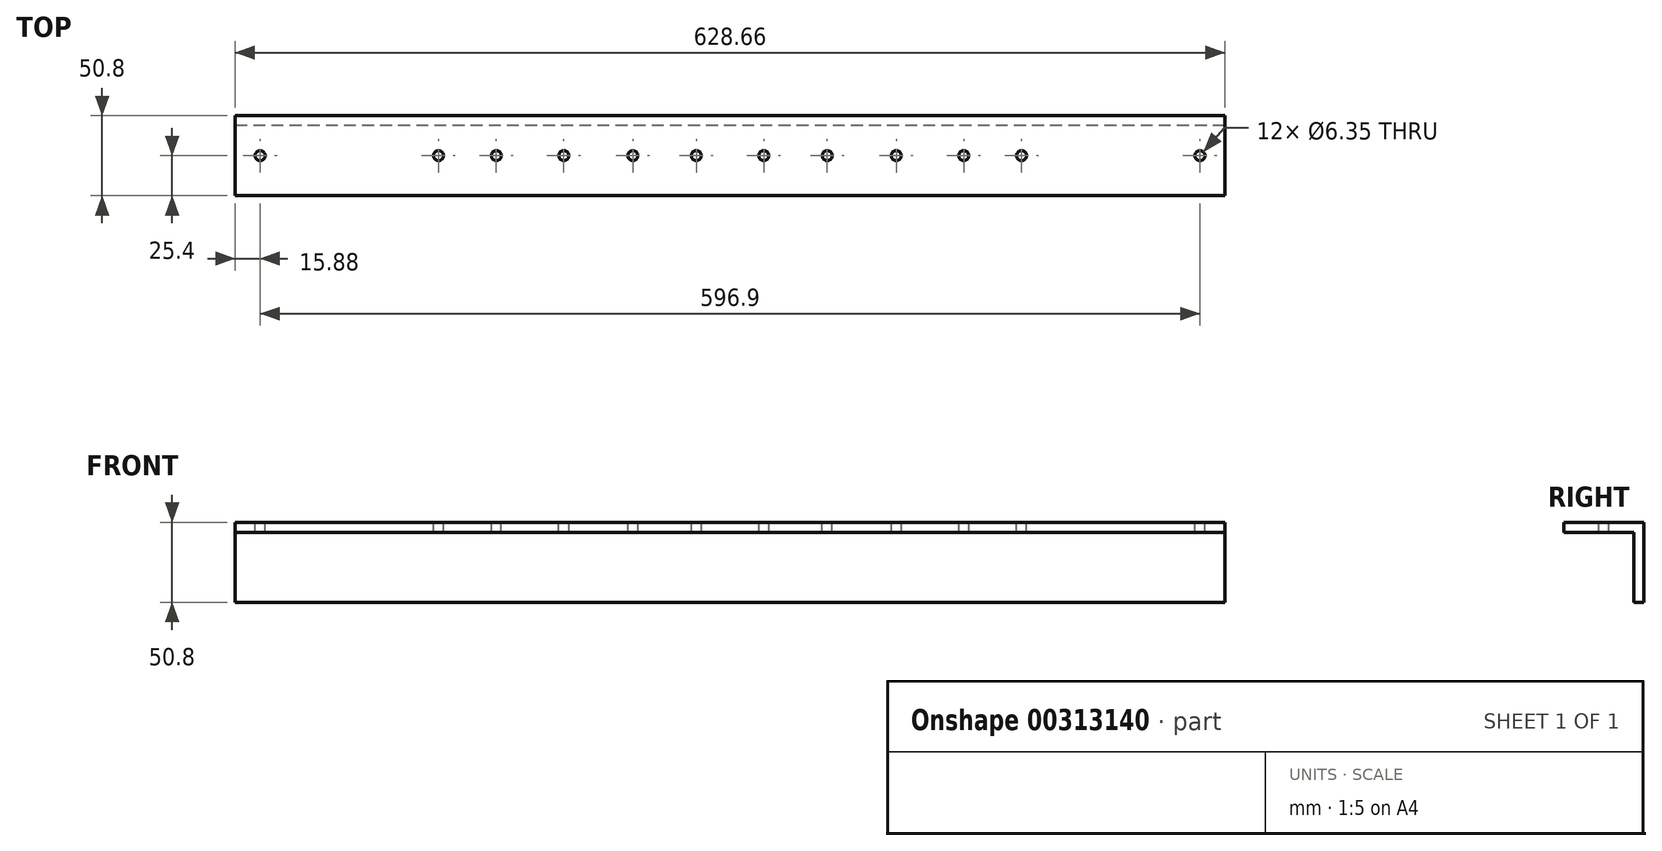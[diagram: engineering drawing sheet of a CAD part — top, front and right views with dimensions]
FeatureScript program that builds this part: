
annotation { "Feature Type Name" : "Feature", "Feature Type Description" : "" }
export const myFeature = defineFeature(function(context is Context, id is Id, definition is map)
    precondition{}
    {
        {
            var Q0;
            Q0=qCreatedBy(makeId("Right.planeOp"),FACE);
            var sketch = newSketch(context, id + "F0", { "sketchPlane" : qUnion([Q0])});
            skLineSegment(sketch, "E0", {"start": v(0, 0) * mm, "end": v(0, 44.45) * mm});
            skLineSegment(sketch, "E1", {"start": v(0, 44.45) * mm, "end": v(-44.45, 44.45) * mm});
            skLineSegment(sketch, "E2", {"start": v(-44.45, 44.45) * mm, "end": v(-44.45, 50.8) * mm});
            skLineSegment(sketch, "E3", {"start": v(-44.45, 50.8) * mm, "end": v(6.35, 50.8) * mm});
            skLineSegment(sketch, "E4", {"start": v(6.35, 50.8) * mm, "end": v(6.35, 0) * mm});
            skLineSegment(sketch, "E5", {"start": v(6.35, 0) * mm, "end": v(0, 0) * mm});
            skSolve(sketch);
        }
        {
            var Q0;
            Q0=qSketchRegion(id+"F0",true);
            extrude(context, id + "F1", {"entities" : qUnion([Q0]), "endBound" : BoundingType.SYMMETRIC, "depth" : 628.65 * mm});
        }
        {
            var Q0;
            Q0=makeQuery(id+"F1.opExtrude","SWEPT_FACE",FACE,{"disambiguationData":[OSD([sQuery(id+"F0.wireOp",EDGE,"E3")])]});
            var sketch = newSketch(context, id + "F2", { "sketchPlane" : qUnion([Q0])});
            skCircle(sketch, "E6", {"center": v(-298.45, -19.05) * mm, "radius": 3.18 * mm});
            skPoint(sketch, "E6.centerSnap0", {"position": v(-314.33, -19.05) * mm});
            skCircle(sketch, "E7", {"center": v(-105.57, -19.05) * mm, "radius": 3.18 * mm});
            skCircle(sketch, "E8", {"center": v(298.45, -19.05) * mm, "radius": 3.18 * mm});
            skCircle(sketch, "E9", {"center": v(-148.43, -19.05) * mm, "radius": 3.18 * mm});
            skCircle(sketch, "E10.1.0.0", {"center": v(-21.43, -19.05) * mm, "radius": 3.18 * mm});
            skCircle(sketch, "E10.1.0.1", {"center": v(21.43, -19.05) * mm, "radius": 3.18 * mm});
            skCircle(sketch, "E10.2.0.0", {"center": v(105.57, -19.05) * mm, "radius": 3.18 * mm});
            skCircle(sketch, "E10.2.0.1", {"center": v(148.43, -19.05) * mm, "radius": 3.18 * mm});
            skLineSegment(sketch, "E10.direction1", {"start": v(-148.43, -19.05) * mm, "end": v(-21.43, -19.05) * mm, "construction": true});
            skLineSegment(sketch, "E11", {"start": v(105.57, -19.05) * mm, "end": v(148.43, -19.05) * mm, "construction": true});
            skPoint(sketch, "E12", {"position": v(127, -19.05) * mm});
            skLineSegment(sketch, "E13", {"start": v(-21.43, -19.05) * mm, "end": v(21.43, -19.05) * mm, "construction": true});
            skPoint(sketch, "E14", {"position": v(0, -19.05) * mm});
            skSolve(sketch);
        }
        {
            var Q0;
            Q0=qSketchRegion(id+"F2",true);
            extrude(context, id + "F3", {"entities" : qUnion([Q0]), "operationType" : NewBodyOperationType.REMOVE, "endBound" : BoundingType.THROUGH_ALL, "oppositeDirection" : true, "depth" : 25.4 * mm});
        }
        {
            var Q0;
            Q0=makeQuery(id+"F1.opExtrude","SWEPT_FACE",FACE,{"disambiguationData":[OSD([sQuery(id+"F0.wireOp",EDGE,"E3")])]});
            var sketch = newSketch(context, id + "F4", { "sketchPlane" : qUnion([Q0])});
            skCircle(sketch, "E15", {"center": v(-185.17, -19.05) * mm, "radius": 3.18 * mm});
            skCircle(sketch, "E16", {"center": v(-61.72, -19.05) * mm, "radius": 3.18 * mm});
            skCircle(sketch, "E17", {"center": v(61.72, -19.05) * mm, "radius": 3.18 * mm});
            skCircle(sketch, "E18", {"center": v(185.17, -19.05) * mm, "radius": 3.18 * mm});
            skLineSegment(sketch, "E19", {"start": v(-185.17, -19.05) * mm, "end": v(-61.72, -19.05) * mm, "construction": true});
            skLineSegment(sketch, "E20", {"start": v(-61.72, -19.05) * mm, "end": v(61.72, -19.05) * mm, "construction": true});
            skLineSegment(sketch, "E21", {"start": v(61.72, -19.05) * mm, "end": v(185.17, -19.05) * mm, "construction": true});
            skPoint(sketch, "E22", {"position": v(-123.44, -19.05) * mm});
            skPoint(sketch, "E23", {"position": v(0, -19.05) * mm});
            skPoint(sketch, "E24", {"position": v(123.44, -19.05) * mm});
            skSolve(sketch);
        }
        {
            var Q0;
            Q0 = qSketchRegion(id + "F4", true);
            extrude(context, id + "F5", {"entities" : qUnion([Q0]), "operationType" : NewBodyOperationType.REMOVE, "endBound" : BoundingType.THROUGH_ALL, "oppositeDirection" : true, "depth" : 25.4 * mm});
        }
    });
